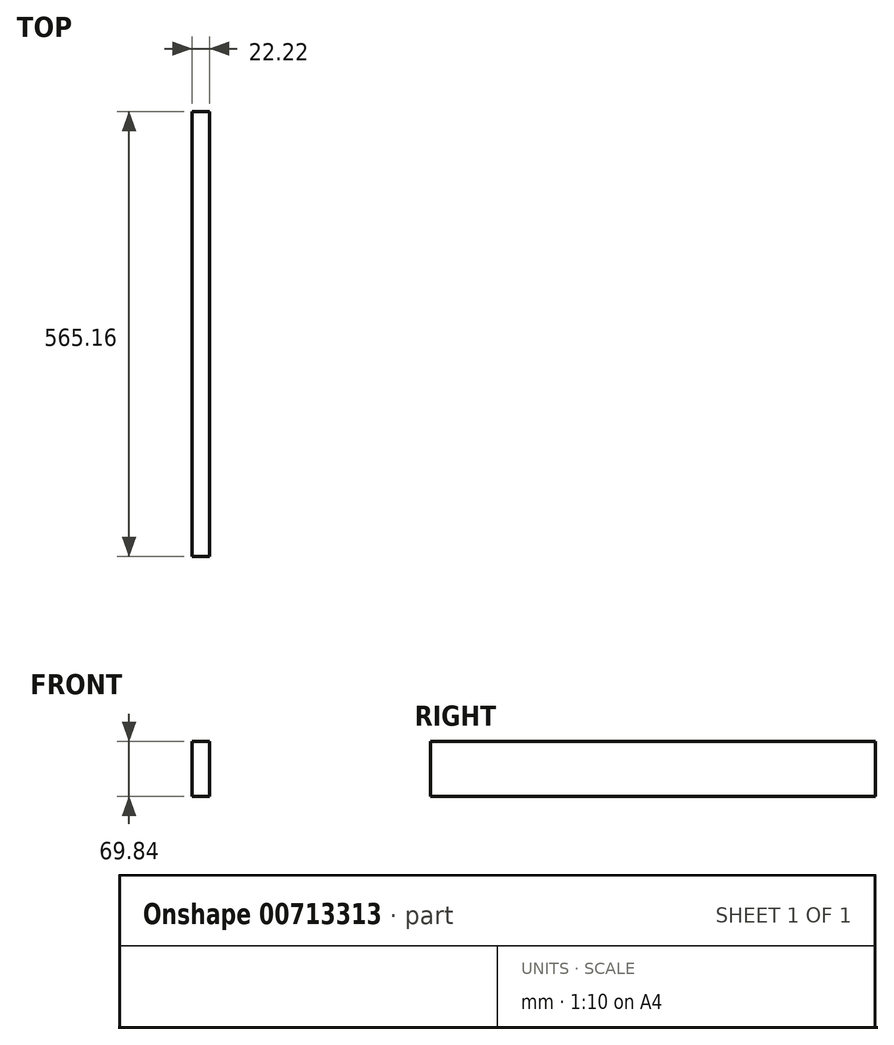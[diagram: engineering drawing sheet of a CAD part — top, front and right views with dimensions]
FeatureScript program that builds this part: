
annotation { "Feature Type Name" : "Feature", "Feature Type Description" : "" }
export const myFeature = defineFeature(function(context is Context, id is Id, definition is map)
    precondition{}
    {
        {
            var Q0;
            Q0=qCreatedBy(makeId("Top.planeOp"),FACE);
            var sketch = newSketch(context, id + "F0", { "sketchPlane" : qUnion([Q0])});
            skLineSegment(sketch, "E0.bottom", {"start": v(11.11, -282.58) * mm, "end": v(-11.11, -282.58) * mm});
            skLineSegment(sketch, "E0.top", {"start": v(11.11, 282.58) * mm, "end": v(-11.11, 282.58) * mm});
            skLineSegment(sketch, "E0.left", {"start": v(11.11, -282.58) * mm, "end": v(11.11, 282.58) * mm});
            skLineSegment(sketch, "E0.right", {"start": v(-11.11, -282.58) * mm, "end": v(-11.11, 282.58) * mm});
            skPoint(sketch, "E0.middle", {"position": v(0, 0) * mm});
            skSolve(sketch);
        }
        {
            var Q0;
            Q0 = qSketchRegion(id + "F0", true);
            extrude(context, id + "F1", {"entities" : qUnion([Q0]), "endBound" : BoundingType.SYMMETRIC, "depth" : 69.85 * mm, "offsetDistance" : 25.4 * mm});
        }
    });
